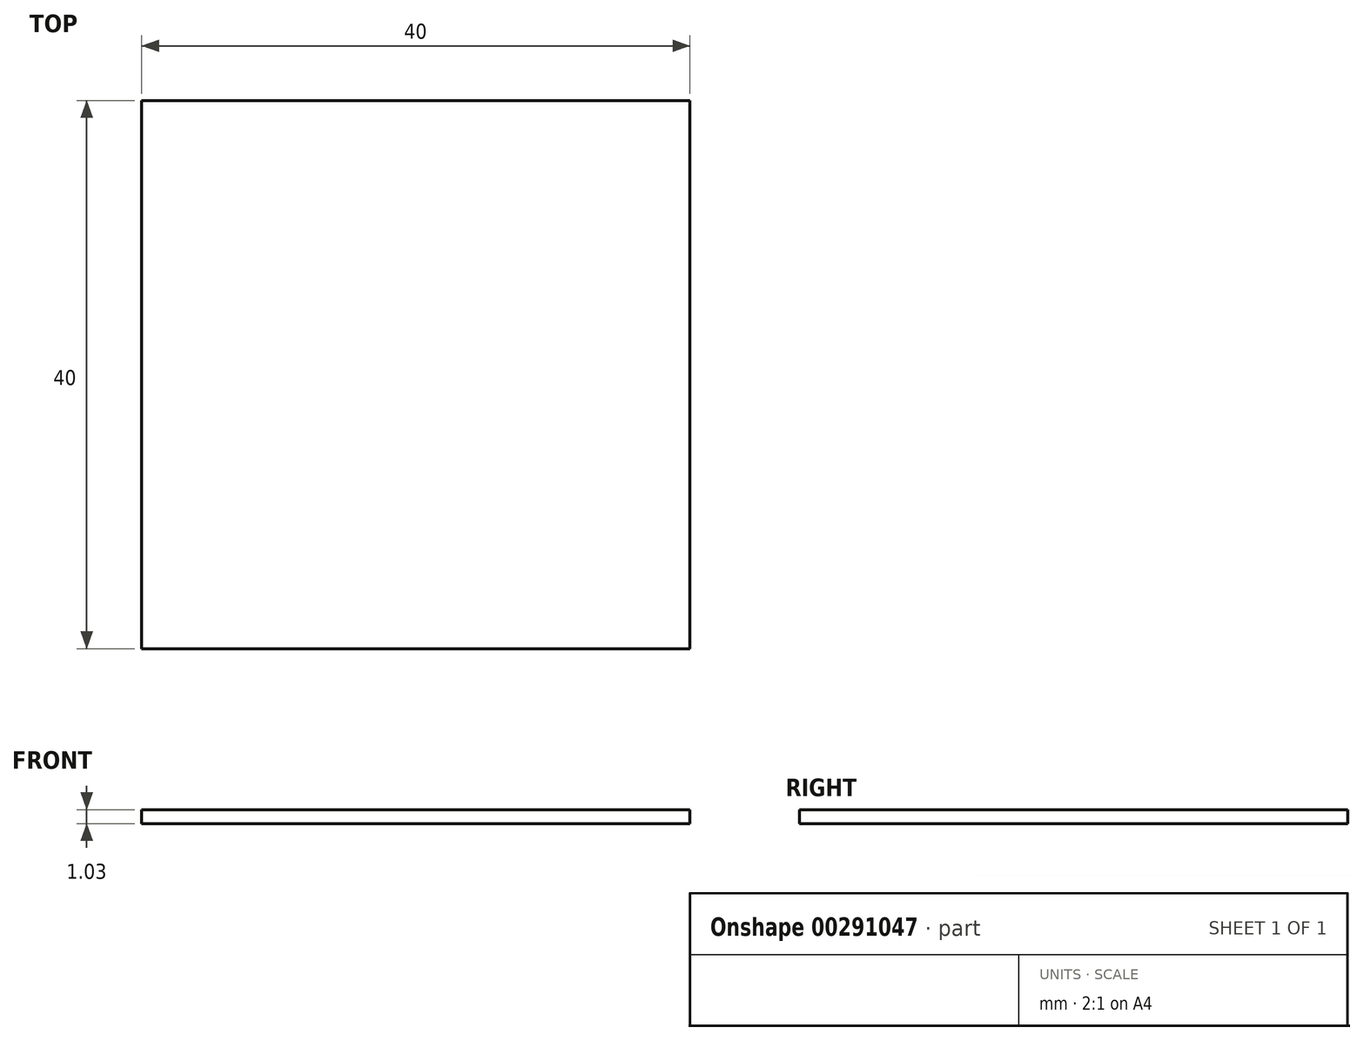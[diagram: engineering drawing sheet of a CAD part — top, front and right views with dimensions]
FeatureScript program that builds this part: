
annotation { "Feature Type Name" : "Feature", "Feature Type Description" : "" }
export const myFeature = defineFeature(function(context is Context, id is Id, definition is map)
    precondition{}
    {
        {
            var Q0;
            Q0=qCreatedBy(makeId("Top.planeOp"),FACE);
            var sketch = newSketch(context, id + "F0", { "sketchPlane" : qUnion([Q0])});
            skLineSegment(sketch, "E0.bottom", {"start": v(-18.48, 18.86) * mm, "end": v(21.52, 18.86) * mm});
            skLineSegment(sketch, "E0.top", {"start": v(-18.48, -21.14) * mm, "end": v(21.52, -21.14) * mm});
            skLineSegment(sketch, "E0.left", {"start": v(-18.48, 18.86) * mm, "end": v(-18.48, -21.14) * mm});
            skLineSegment(sketch, "E0.right", {"start": v(21.52, 18.86) * mm, "end": v(21.52, -21.14) * mm});
            skSolve(sketch);
        }
        {
            var Q0;
            Q0=makeQuery(id+"F0.imprint","IMPRINT",FACE,{"disambiguationData":[TD([[makeQuery(id+"F0.imprint","IMPRINT",EDGE,{"derivedFrom":sQuery(id+"F0.wireOp",EDGE,"E0.bottom")}),-1.0]])]});
            extrude(context, id + "F1", {"entities" : qUnion([Q0]), "depth" : 1.03 * mm});
        }
    });
